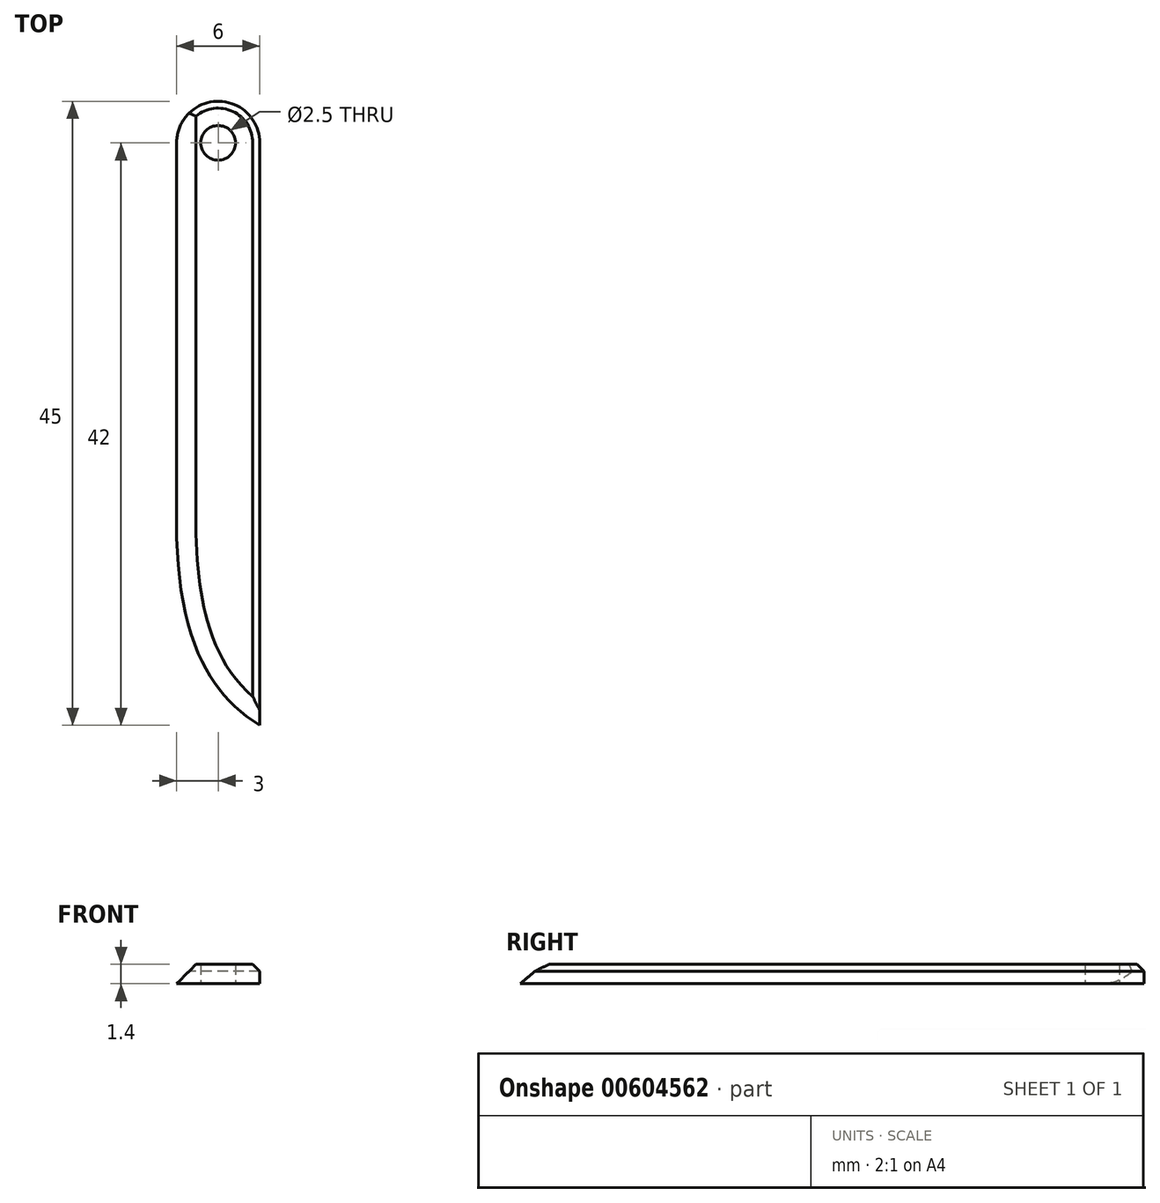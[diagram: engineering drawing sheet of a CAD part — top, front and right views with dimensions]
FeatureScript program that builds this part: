
annotation { "Feature Type Name" : "Feature", "Feature Type Description" : "" }
export const myFeature = defineFeature(function(context is Context, id is Id, definition is map)
    precondition{}
    {
        {
            var Q0;
            Q0=qCreatedBy(makeId("Top.planeOp"),FACE);
            var sketch = newSketch(context, id + "F0", { "sketchPlane" : qUnion([Q0])});
            skLineSegment(sketch, "E0.left", {"start": v(-3, 22) * mm, "end": v(-3, -5.5) * mm});
            skLineSegment(sketch, "E0.right", {"start": v(3, 22) * mm, "end": v(3, -20) * mm});
            skFitSpline(sketch, "E1", {"points": [v(-3, -5.5) * mm, v(3, -20) * mm], "startDerivative": vector(0, -25.24) * mm, "endDerivative": vector(10.35, -6.18) * mm});
            skArc(sketch, "E2", {"start": v(3, 22) * mm, "mid": v(0, 25) * mm, "end": v(-3, 22) * mm});
            skCircle(sketch, "E3", {"center": v(0, 22) * mm, "radius": 1.25 * mm});
            skSolve(sketch);
        }
        {
            var Q0;
            Q0=makeQuery(id+"F0.imprint","IMPRINT",FACE,{"disambiguationData":[TD([[makeQuery(id+"F0.imprint","IMPRINT",EDGE,{"derivedFrom":sQuery(id+"F0.wireOp",EDGE,"E0.left")}),1.0]])]});
            extrude(context, id + "F1", {"entities" : qUnion([Q0]), "depth" : 1.4 * mm, "offsetDistance" : 25 * mm});
        }
        {
            var Q0;
            Q0=makeQuery(id+"F1.opExtrude","CAP_EDGE",EDGE,{"disambiguationData":[OSD([sQuery(id+"F0.wireOp",EDGE,"E1")])],"isStart":false});
            var Q1;
            Q1=makeQuery(id+"F1.opExtrude","CAP_EDGE",EDGE,{"disambiguationData":[OSD([sQuery(id+"F0.wireOp",EDGE,"E0.left")])],"isStart":false});
            chamfer(context, id + "F2", {"entities" : qUnion([Q0, Q1]), "width" : 1.4 * mm});
        }
        {
            var Q0;
            Q0=makeQuery(id+"F1.opExtrude","CAP_EDGE",EDGE,{"disambiguationData":[OSD([sQuery(id+"F0.wireOp",EDGE,"E0.right")])],"isStart":false});
            chamfer(context, id + "F3", {"entities" : qUnion([Q0]), "width" : 0.5 * mm, "tangentPropagation" : true});
        }
    });
